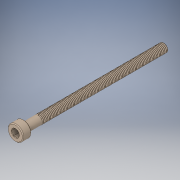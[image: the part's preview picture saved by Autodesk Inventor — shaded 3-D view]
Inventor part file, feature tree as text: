
AUTODESK INVENTOR PART (.ipt)
format: ipt  version: 2019.4 (Build 234330000, 330)  size: 773,632 bytes
history: mixed  units: mm
features: chamfer x1, imported_body x1
ambient origin geometry x8: Origin, YZ Plane, XZ Plane, XY Plane, X Axis, Y Axis, Z Axis, Center Point
bodies: Solid1 (imported_parasolid)
feature tree (2):
  chamfer  "Chamfer1"  [1 undecoded]
  imported_body  NMx_Import_Brep_tag  [imported B-rep: ~3 faces, bbox_mm=None]
note: 1 required parameter value undecoded (feature->parameter linkage not recoverable at this tier; creation-order binding heuristic only, values carry confidence <= 0.55)
